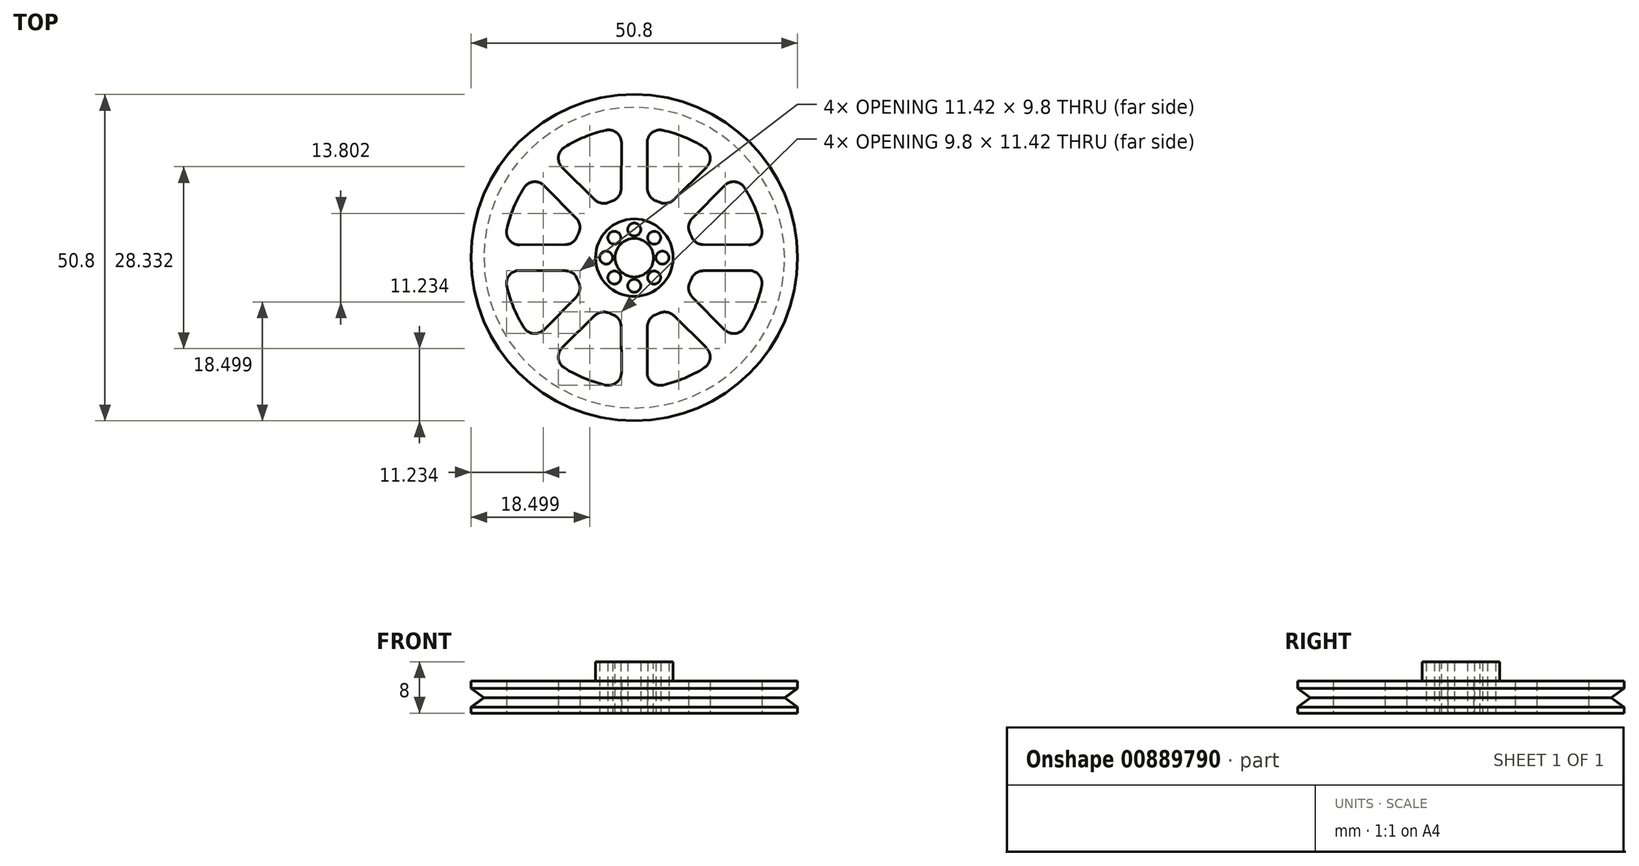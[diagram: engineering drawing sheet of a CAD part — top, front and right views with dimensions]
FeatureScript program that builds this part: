
annotation { "Feature Type Name" : "Feature", "Feature Type Description" : "" }
export const myFeature = defineFeature(function(context is Context, id is Id, definition is map)
    precondition{}
    {
        {
            var Q0;
            Q0=qCreatedBy(makeId("Top.planeOp"),FACE);
            var sketch = newSketch(context, id + "F0", { "sketchPlane" : qUnion([Q0])});
            skCircle(sketch, "E0", {"center": v(0, 0) * mm, "radius": 25.4 * mm});
            skCircle(sketch, "E1", {"center": v(0, 0) * mm, "radius": 3.12 * mm});
            skArc(sketch, "E2.0", {"start": v(-4.44, 19.83) * mm, "mid": v(-7.78, 18.77) * mm, "end": v(-10.88, 17.16) * mm});
            skArc(sketch, "E3.0", {"start": v(-3.34, 8.87) * mm, "mid": v(-3.63, 8.75) * mm, "end": v(-3.9, 8.63) * mm});
            skLineSegment(sketch, "E4.0", {"start": v(-2, 17.87) * mm, "end": v(-2.04, 10.73) * mm});
            skLineSegment(sketch, "E5.0", {"start": v(2, 17.87) * mm, "end": v(2.04, 10.73) * mm});
            skPoint(sketch, "E6.orphan", {"position": v(0, 22.85) * mm});
            skPoint(sketch, "E7.visualSharp", {"position": v(-1.99, 20.22) * mm});
            skArc(sketch, "E7.filletArc", {"start": v(-2, 17.87) * mm, "mid": v(-2.74, 19.44) * mm, "end": v(-4.44, 19.83) * mm});
            skPoint(sketch, "E8.visualSharp", {"position": v(1.99, 20.22) * mm});
            skArc(sketch, "E8.filletArc", {"start": v(4.44, 19.83) * mm, "mid": v(2.74, 19.44) * mm, "end": v(2, 17.87) * mm});
            skPoint(sketch, "E9.visualSharp", {"position": v(-2.05, 9.25) * mm});
            skArc(sketch, "E9.filletArc", {"start": v(-3.34, 8.87) * mm, "mid": v(-2.4, 9.6) * mm, "end": v(-2.04, 10.73) * mm});
            skPoint(sketch, "E10.visualSharp", {"position": v(2.05, 9.25) * mm});
            skArc(sketch, "E10.filletArc", {"start": v(2.04, 10.73) * mm, "mid": v(2.4, 9.6) * mm, "end": v(3.34, 8.87) * mm});
            skArc(sketch, "E11.1.0", {"start": v(-14.05, 11.22) * mm, "mid": v(-15.68, 11.8) * mm, "end": v(-17.16, 10.88) * mm});
            skLineSegment(sketch, "E11.1.1", {"start": v(-14.05, 11.22) * mm, "end": v(-9.03, 6.14) * mm});
            skArc(sketch, "E11.1.2", {"start": v(-8.63, 3.9) * mm, "mid": v(-8.48, 5.09) * mm, "end": v(-9.03, 6.14) * mm});
            skArc(sketch, "E11.1.3", {"start": v(-10.88, 17.16) * mm, "mid": v(-11.8, 15.68) * mm, "end": v(-11.22, 14.05) * mm});
            skLineSegment(sketch, "E11.1.4", {"start": v(-11.22, 14.05) * mm, "end": v(-6.14, 9.03) * mm});
            skArc(sketch, "E11.1.5", {"start": v(-6.14, 9.03) * mm, "mid": v(-5.09, 8.48) * mm, "end": v(-3.9, 8.63) * mm});
            skArc(sketch, "E11.2.0", {"start": v(-17.87, -2) * mm, "mid": v(-19.44, -2.74) * mm, "end": v(-19.83, -4.44) * mm});
            skLineSegment(sketch, "E11.2.1", {"start": v(-17.87, -2) * mm, "end": v(-10.73, -2.04) * mm});
            skArc(sketch, "E11.2.2", {"start": v(-8.87, -3.34) * mm, "mid": v(-9.6, -2.4) * mm, "end": v(-10.73, -2.04) * mm});
            skArc(sketch, "E11.2.3", {"start": v(-19.83, 4.44) * mm, "mid": v(-19.44, 2.74) * mm, "end": v(-17.87, 2) * mm});
            skLineSegment(sketch, "E11.2.4", {"start": v(-17.87, 2) * mm, "end": v(-10.73, 2.04) * mm});
            skArc(sketch, "E11.2.5", {"start": v(-10.73, 2.04) * mm, "mid": v(-9.6, 2.4) * mm, "end": v(-8.87, 3.34) * mm});
            skArc(sketch, "E11.3.0", {"start": v(-11.22, -14.05) * mm, "mid": v(-11.8, -15.68) * mm, "end": v(-10.88, -17.16) * mm});
            skLineSegment(sketch, "E11.3.1", {"start": v(-11.22, -14.05) * mm, "end": v(-6.14, -9.03) * mm});
            skArc(sketch, "E11.3.2", {"start": v(-3.9, -8.63) * mm, "mid": v(-5.09, -8.48) * mm, "end": v(-6.14, -9.03) * mm});
            skArc(sketch, "E11.3.3", {"start": v(-17.16, -10.88) * mm, "mid": v(-15.68, -11.8) * mm, "end": v(-14.05, -11.22) * mm});
            skLineSegment(sketch, "E11.3.4", {"start": v(-14.05, -11.22) * mm, "end": v(-9.03, -6.14) * mm});
            skArc(sketch, "E11.3.5", {"start": v(-9.03, -6.14) * mm, "mid": v(-8.48, -5.09) * mm, "end": v(-8.63, -3.9) * mm});
            skArc(sketch, "E11.4.0", {"start": v(2, -17.87) * mm, "mid": v(2.74, -19.44) * mm, "end": v(4.44, -19.83) * mm});
            skLineSegment(sketch, "E11.4.1", {"start": v(2, -17.87) * mm, "end": v(2.04, -10.73) * mm});
            skArc(sketch, "E11.4.2", {"start": v(3.34, -8.87) * mm, "mid": v(2.4, -9.6) * mm, "end": v(2.04, -10.73) * mm});
            skArc(sketch, "E11.4.3", {"start": v(-4.44, -19.83) * mm, "mid": v(-2.74, -19.44) * mm, "end": v(-2, -17.87) * mm});
            skLineSegment(sketch, "E11.4.4", {"start": v(-2, -17.87) * mm, "end": v(-2.04, -10.73) * mm});
            skArc(sketch, "E11.4.5", {"start": v(-2.04, -10.73) * mm, "mid": v(-2.4, -9.6) * mm, "end": v(-3.34, -8.87) * mm});
            skArc(sketch, "E11.5.0", {"start": v(14.05, -11.22) * mm, "mid": v(15.68, -11.8) * mm, "end": v(17.16, -10.88) * mm});
            skLineSegment(sketch, "E11.5.1", {"start": v(14.05, -11.22) * mm, "end": v(9.03, -6.14) * mm});
            skArc(sketch, "E11.5.2", {"start": v(8.63, -3.9) * mm, "mid": v(8.48, -5.09) * mm, "end": v(9.03, -6.14) * mm});
            skArc(sketch, "E11.5.3", {"start": v(10.88, -17.16) * mm, "mid": v(11.8, -15.68) * mm, "end": v(11.22, -14.05) * mm});
            skLineSegment(sketch, "E11.5.4", {"start": v(11.22, -14.05) * mm, "end": v(6.14, -9.03) * mm});
            skArc(sketch, "E11.5.5", {"start": v(6.14, -9.03) * mm, "mid": v(5.09, -8.48) * mm, "end": v(3.9, -8.63) * mm});
            skArc(sketch, "E11.6.0", {"start": v(17.87, 2) * mm, "mid": v(19.44, 2.74) * mm, "end": v(19.83, 4.44) * mm});
            skLineSegment(sketch, "E11.6.1", {"start": v(17.87, 2) * mm, "end": v(10.73, 2.04) * mm});
            skArc(sketch, "E11.6.2", {"start": v(8.87, 3.34) * mm, "mid": v(9.6, 2.4) * mm, "end": v(10.73, 2.04) * mm});
            skArc(sketch, "E11.6.3", {"start": v(19.83, -4.44) * mm, "mid": v(19.44, -2.74) * mm, "end": v(17.87, -2) * mm});
            skLineSegment(sketch, "E11.6.4", {"start": v(17.87, -2) * mm, "end": v(10.73, -2.04) * mm});
            skArc(sketch, "E11.6.5", {"start": v(10.73, -2.04) * mm, "mid": v(9.6, -2.4) * mm, "end": v(8.87, -3.34) * mm});
            skArc(sketch, "E11.7.0", {"start": v(11.22, 14.05) * mm, "mid": v(11.8, 15.68) * mm, "end": v(10.88, 17.16) * mm});
            skLineSegment(sketch, "E11.7.1", {"start": v(11.22, 14.05) * mm, "end": v(6.14, 9.03) * mm});
            skArc(sketch, "E11.7.2", {"start": v(3.9, 8.63) * mm, "mid": v(5.09, 8.48) * mm, "end": v(6.14, 9.03) * mm});
            skArc(sketch, "E11.7.3", {"start": v(17.16, 10.88) * mm, "mid": v(15.68, 11.8) * mm, "end": v(14.05, 11.22) * mm});
            skLineSegment(sketch, "E11.7.4", {"start": v(14.05, 11.22) * mm, "end": v(9.03, 6.14) * mm});
            skArc(sketch, "E11.7.5", {"start": v(9.03, 6.14) * mm, "mid": v(8.48, 5.09) * mm, "end": v(8.63, 3.9) * mm});
            skArc(sketch, "E12.trimOffspring", {"start": v(-17.16, 10.88) * mm, "mid": v(-18.77, 7.78) * mm, "end": v(-19.83, 4.44) * mm});
            skArc(sketch, "E13.trimOffspring", {"start": v(-8.63, 3.9) * mm, "mid": v(-8.75, 3.63) * mm, "end": v(-8.87, 3.34) * mm});
            skArc(sketch, "E14.trimOffspring", {"start": v(-8.87, -3.34) * mm, "mid": v(-8.75, -3.63) * mm, "end": v(-8.63, -3.9) * mm});
            skArc(sketch, "E15.trimOffspring", {"start": v(-19.83, -4.44) * mm, "mid": v(-18.77, -7.78) * mm, "end": v(-17.16, -10.88) * mm});
            skArc(sketch, "E16.trimOffspring", {"start": v(-10.88, -17.16) * mm, "mid": v(-7.78, -18.77) * mm, "end": v(-4.44, -19.83) * mm});
            skArc(sketch, "E17.trimOffspring", {"start": v(-3.9, -8.63) * mm, "mid": v(-3.63, -8.75) * mm, "end": v(-3.34, -8.87) * mm});
            skArc(sketch, "E18.trimOffspring", {"start": v(3.34, -8.87) * mm, "mid": v(3.63, -8.75) * mm, "end": v(3.9, -8.63) * mm});
            skArc(sketch, "E19.trimOffspring", {"start": v(8.63, -3.9) * mm, "mid": v(8.75, -3.63) * mm, "end": v(8.87, -3.34) * mm});
            skArc(sketch, "E20.trimOffspring", {"start": v(8.87, 3.34) * mm, "mid": v(8.75, 3.63) * mm, "end": v(8.63, 3.9) * mm});
            skArc(sketch, "E21.trimOffspring", {"start": v(3.9, 8.63) * mm, "mid": v(3.63, 8.75) * mm, "end": v(3.34, 8.87) * mm});
            skArc(sketch, "E22.trimOffspring", {"start": v(10.88, 17.16) * mm, "mid": v(7.78, 18.77) * mm, "end": v(4.44, 19.83) * mm});
            skArc(sketch, "E23.trimOffspring", {"start": v(19.83, 4.44) * mm, "mid": v(18.77, 7.78) * mm, "end": v(17.16, 10.88) * mm});
            skArc(sketch, "E24.trimOffspring", {"start": v(17.16, -10.88) * mm, "mid": v(18.77, -7.78) * mm, "end": v(19.83, -4.44) * mm});
            skArc(sketch, "E25.trimOffspring", {"start": v(4.44, -19.83) * mm, "mid": v(7.78, -18.77) * mm, "end": v(10.88, -17.16) * mm});
            skSolve(sketch);
        }
        {
            var Q0;
            Q0=makeQuery(id+"F0.imprint","IMPRINT",FACE,{"disambiguationData":[TD([[makeQuery(id+"F0.imprint","IMPRINT",EDGE,{"derivedFrom":sQuery(id+"F0.wireOp",EDGE,"E0")}),1.0]])]});
            extrude(context, id + "F1", {"entities" : qUnion([Q0]), "depth" : 5 * mm, "offsetDistance" : 25.4 * mm});
        }
        {
            var Q0;
            Q0=qCreatedBy(makeId("Top.planeOp"),FACE);
            var sketch = newSketch(context, id + "F2", { "sketchPlane" : qUnion([Q0])});
            skCircle(sketch, "E26", {"center": v(0, 0) * mm, "radius": 6.03 * mm});
            skSolve(sketch);
        }
        {
            var Q0;
            Q0=makeQuery(id+"F2.imprint","IMPRINT",FACE,{"disambiguationData":[TD([[makeQuery(id+"F2.imprint","IMPRINT",EDGE,{"derivedFrom":sQuery(id+"F2.wireOp",EDGE,"E26")}),1.0]])]});
            extrude(context, id + "F3", {"entities" : qUnion([Q0]), "operationType" : NewBodyOperationType.ADD, "depth" : 8 * mm, "offsetDistance" : 25.4 * mm});
        }
        {
            var Q0;
            Q0=makeQuery(id+"F3.opExtrude","CAP_FACE",FACE,{"disambiguationData":[OSD([sQuery(id+"F2.wireOp",EDGE,"E26")])],"isStart":false});
            var sketch = newSketch(context, id + "F4", { "sketchPlane" : qUnion([Q0])});
            skCircle(sketch, "E27", {"center": v(0, 0) * mm, "radius": 3 * mm});
            skSolve(sketch);
        }
        {
            var Q0;
            Q0=makeQuery(id+"F4.imprint","IMPRINT",FACE,{"disambiguationData":[TD([[makeQuery(id+"F4.imprint","IMPRINT",EDGE,{"derivedFrom":sQuery(id+"F4.wireOp",EDGE,"E27")}),1.0]])]});
            extrude(context, id + "F5", {"entities" : qUnion([Q0]), "operationType" : NewBodyOperationType.REMOVE, "endBound" : BoundingType.THROUGH_ALL, "oppositeDirection" : true, "depth" : 25.4 * mm, "offsetDistance" : 25.4 * mm});
        }
        {
            var Q0;
            Q0=qCreatedBy(makeId("Right.planeOp"),FACE);
            var sketch = newSketch(context, id + "F6", { "sketchPlane" : qUnion([Q0])});
            skLineSegment(sketch, "E28", {"start": v(25.4, 2.4) * mm, "end": v(23.4, 2.4) * mm});
            skLineSegment(sketch, "E29", {"start": v(23.4, 2.4) * mm, "end": v(25.46, 3.9) * mm});
            skLineSegment(sketch, "E30", {"start": v(25.46, 3.9) * mm, "end": v(25.4, 2.4) * mm});
            skLineSegment(sketch, "E31.MirrorCS", {"start": v(23.4, 2.4) * mm, "end": v(25.46, 0.9) * mm});
            skLineSegment(sketch, "E32.MirrorCS", {"start": v(25.46, 0.9) * mm, "end": v(25.4, 2.4) * mm});
            skLineSegment(sketch, "E33", {"start": v(0, 19.4) * mm, "end": v(0, -3.2) * mm, "construction": true});
            skSolve(sketch);
        }
        {
            var Q0;
            Q0=qSketchRegion(id+"F6",true);
            var Q1;
            Q1=sQuery(id+"F6.wireOp",EDGE,"E33");
            revolve(context, id + "F7", {"operationType" : NewBodyOperationType.REMOVE, "surfaceOperationType" : NewSurfaceOperationType.NEW, "entities" : qUnion([Q0]), "axis" : qUnion([Q1]), "revolveType" : RevolveType.FULL, "oppositeDirection" : true});
        }
        {
            var Q0;
            Q0=qCreatedBy(makeId("Top.planeOp"),FACE);
            var sketch = newSketch(context, id + "F8", { "sketchPlane" : qUnion([Q0])});
            skCircle(sketch, "E34", {"center": v(0, 4.38) * mm, "radius": 1 * mm});
            skCircle(sketch, "E35.1.0", {"center": v(-3.1, 3.1) * mm, "radius": 1 * mm});
            skCircle(sketch, "E35.2.0", {"center": v(-4.38, 0) * mm, "radius": 1 * mm});
            skPoint(sketch, "E35.center", {"position": v(0, 0) * mm});
            skCircle(sketch, "E36.1.3.0", {"center": v(-3.1, -3.1) * mm, "radius": 1 * mm});
            skCircle(sketch, "E36.1.4.0", {"center": v(0, -4.38) * mm, "radius": 1 * mm});
            skCircle(sketch, "E36.1.5.0", {"center": v(3.1, -3.1) * mm, "radius": 1 * mm});
            skCircle(sketch, "E36.1.6.0", {"center": v(4.38, 0) * mm, "radius": 1 * mm});
            skCircle(sketch, "E36.1.7.0", {"center": v(3.1, 3.1) * mm, "radius": 1 * mm});
            skSolve(sketch);
        }
        {
            var Q0;
            Q0=qSketchRegion(id+"F8",true);
            extrude(context, id + "F9", {"entities" : qUnion([Q0]), "operationType" : NewBodyOperationType.REMOVE, "endBound" : BoundingType.THROUGH_ALL, "depth" : 25.4 * mm, "offsetDistance" : 25.4 * mm});
        }
    });
